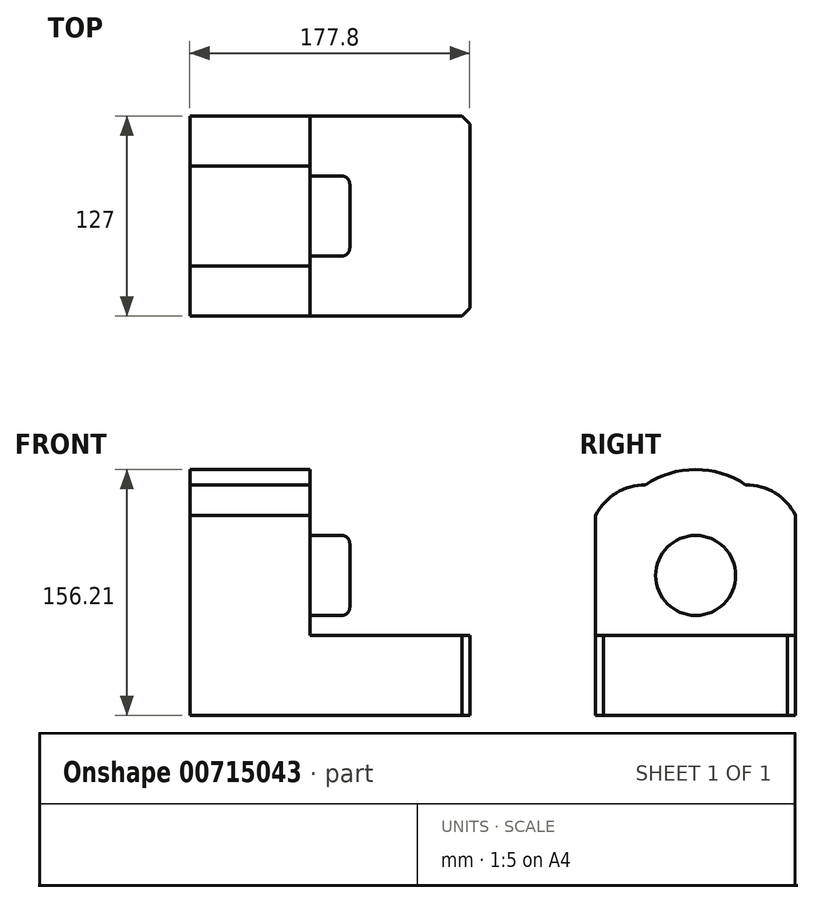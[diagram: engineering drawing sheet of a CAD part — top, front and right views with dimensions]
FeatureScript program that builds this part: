
annotation { "Feature Type Name" : "Feature", "Feature Type Description" : "" }
export const myFeature = defineFeature(function(context is Context, id is Id, definition is map)
    precondition{}
    {
        {
            var Q0;
            Q0=qCreatedBy(makeId("Front.planeOp"),FACE);
            var sketch = newSketch(context, id + "F0", { "sketchPlane" : qUnion([Q0])});
            skLineSegment(sketch, "E0.bottom", {"start": v(-64.09, 66.4) * mm, "end": v(12.11, 66.4) * mm});
            skLineSegment(sketch, "E0.top", {"start": v(-64.09, -9.8) * mm, "end": v(12.11, -9.8) * mm});
            skLineSegment(sketch, "E0.left", {"start": v(-64.09, 66.4) * mm, "end": v(-64.09, -9.8) * mm});
            skLineSegment(sketch, "E0.right", {"start": v(12.11, 66.4) * mm, "end": v(12.11, -9.8) * mm});
            skLineSegment(sketch, "E1.bottom", {"start": v(-64.09, -9.8) * mm, "end": v(113.71, -9.8) * mm});
            skLineSegment(sketch, "E1.top", {"start": v(-64.09, -60.6) * mm, "end": v(113.71, -60.6) * mm});
            skLineSegment(sketch, "E1.left", {"start": v(-64.09, -9.8) * mm, "end": v(-64.09, -60.6) * mm});
            skLineSegment(sketch, "E1.right", {"start": v(113.71, -9.8) * mm, "end": v(113.71, -60.6) * mm});
            skSolve(sketch);
        }
        {
            var Q0;
            Q0=makeQuery(id+"F0.imprint","IMPRINT",FACE,{"disambiguationData":[TD([[makeQuery(id+"F0.imprint","IMPRINT",EDGE,{"derivedFrom":sQuery(id+"F0.wireOp",EDGE,"E1.top")}),1.0]])]});
            var Q1;
            Q1=makeQuery(id+"F0.imprint","IMPRINT",FACE,{"disambiguationData":[TD([[makeQuery(id+"F0.imprint","IMPRINT",EDGE,{"derivedFrom":sQuery(id+"F0.wireOp",EDGE,"E0.bottom")}),-1.0]])]});
            extrude(context, id + "F1", {"entities" : qUnion([Q0, Q1]), "depth" : 127 * mm, "offsetDistance" : 25.4 * mm});
        }
        {
            var Q0;
            Q0=makeQuery(id+"F1.opExtrude","CAP_EDGE",EDGE,{"disambiguationData":[OSD([sQuery(id+"F0.wireOp",EDGE,"E1.right")])],"isStart":false});
            var Q1;
            Q1=makeQuery(id+"F1.opExtrude","CAP_EDGE",EDGE,{"disambiguationData":[OSD([sQuery(id+"F0.wireOp",EDGE,"E1.right")])],"isStart":true});
            chamfer(context, id + "F2", {"entities" : qUnion([Q0, Q1]), "width" : 5.08 * mm, "tangentPropagation" : true});
        }
        {
            var Q0;
            Q0=makeQuery(id+"F1.opExtrude","SWEPT_FACE",FACE,{"disambiguationData":[OSD([sQuery(id+"F0.wireOp",EDGE,"E0.right")])]});
            var sketch = newSketch(context, id + "F3", { "sketchPlane" : qUnion([Q0])});
            skCircle(sketch, "E2", {"center": v(-63.5, 28.3) * mm, "radius": 25.4 * mm});
            skPoint(sketch, "E2.centerSnap0", {"position": v(-63.5, 63.86) * mm});
            skArc(sketch, "E3", {"start": v(-63.5, 66.4) * mm, "mid": v(-95.25, 85.95) * mm, "end": v(-127, 66.4) * mm});
            skArc(sketch, "E4", {"start": v(0, 66.4) * mm, "mid": v(-31.75, 85.95) * mm, "end": v(-63.5, 66.4) * mm});
            skArc(sketch, "E5", {"start": v(-31.75, 85.95) * mm, "mid": v(-63.5, 95.6) * mm, "end": v(-95.25, 85.95) * mm});
            skSolve(sketch);
        }
        {
            var Q0;
            Q0=makeQuery(id+"F3.imprint","IMPRINT",FACE,{"disambiguationData":[TD([[makeQuery(id+"F3.imprint","IMPRINT",EDGE,{"derivedFrom":sQuery(id+"F3.wireOp",EDGE,"E2")}),1.0]])]});
            extrude(context, id + "F4", {"entities" : qUnion([Q0]), "operationType" : NewBodyOperationType.ADD, "depth" : 25.4 * mm, "offsetDistance" : 25.4 * mm});
        }
        {
            var Q0;
            Q0=makeQuery(id+"F4.opExtrude","CAP_FACE",FACE,{"disambiguationData":[OSD([sQuery(id+"F3.wireOp",EDGE,"E2")])],"isStart":false});
            fillet(context, id + "F5", {"entities" : qUnion([Q0]), "radius" : 5.08 * mm, "tangentPropagation" : true, "allowEdgeOverflow" : false});
        }
        {
            var Q0;
            {var subQ0=sQuery(id+"F3.wireOp",EDGE,"E4");var subQ4=makeQuery(id+"F3.imprint","INTERSECT",VERTEX,{"derivedFrom":[subQ0,sQuery(id+"F3.wireOp",EDGE,"E5")]});Q0=makeQuery(id+"F3.imprint","IMPRINT",FACE,{"disambiguationData":[TD([[makeQuery(id+"F3.imprint","IMPRINT",EDGE,{"disambiguationData":[TD([[subQ4,1.0]])],"derivedFrom":subQ0}),1.0]])]});}
            var Q1;
            {var subQ3=sQuery(id+"F3.wireOp",EDGE,"E5");Q1=makeQuery(id+"F3.imprint","IMPRINT",FACE,{"disambiguationData":[TD([[makeQuery(id+"F3.imprint","IMPRINT",EDGE,{"derivedFrom":subQ3}),1.0]])]});}
            var Q2;
            {var subQ0=sQuery(id+"F3.wireOp",EDGE,"E3");var subQ4=makeQuery(id+"F3.imprint","INTERSECT",VERTEX,{"derivedFrom":[subQ0,sQuery(id+"F3.wireOp",EDGE,"E5")]});Q2=makeQuery(id+"F3.imprint","IMPRINT",FACE,{"disambiguationData":[TD([[makeQuery(id+"F3.imprint","IMPRINT",EDGE,{"disambiguationData":[TD([[subQ4,1.0]])],"derivedFrom":subQ0}),1.0]])]});}
            extrude(context, id + "F6", {"entities" : qUnion([Q0, Q1, Q2]), "operationType" : NewBodyOperationType.ADD, "oppositeDirection" : true, "depth" : 76.2 * mm, "offsetDistance" : 25.4 * mm});
        }
    });
